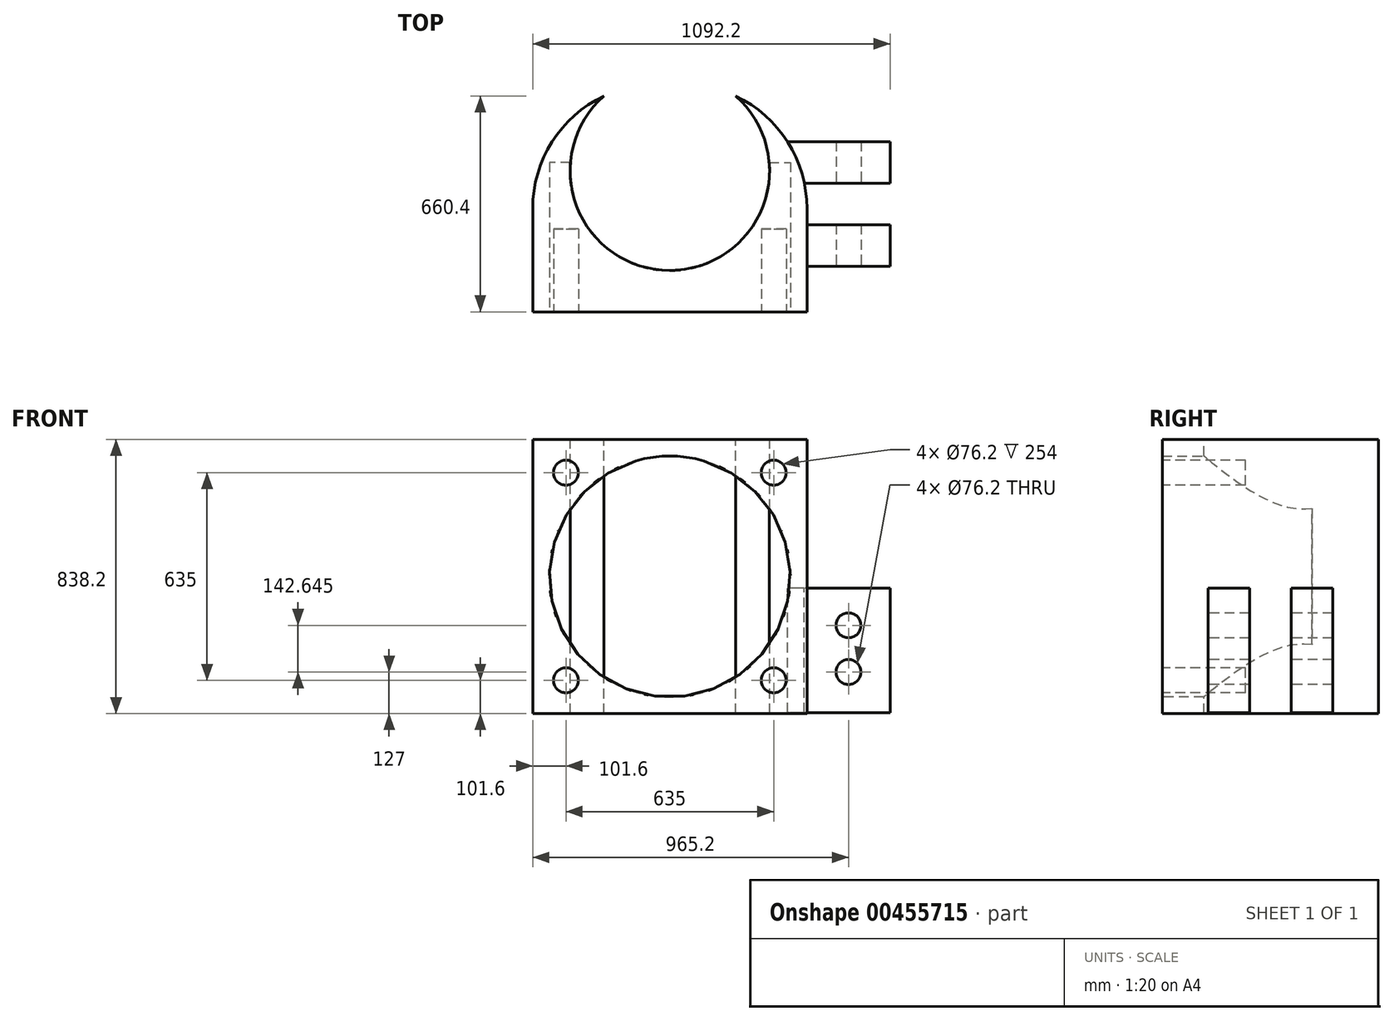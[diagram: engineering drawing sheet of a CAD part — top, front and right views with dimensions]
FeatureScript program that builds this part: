
annotation { "Feature Type Name" : "Feature", "Feature Type Description" : "" }
export const myFeature = defineFeature(function(context is Context, id is Id, definition is map)
    precondition{}
    {
        {
            var Q0;
            Q0=qCreatedBy(makeId("Front.planeOp"),FACE);
            var sketch = newSketch(context, id + "F0", { "sketchPlane" : qUnion([Q0])});
            skLineSegment(sketch, "E0.bottom", {"start": v(-419.1, 419.1) * mm, "end": v(419.1, 419.1) * mm});
            skLineSegment(sketch, "E0.top", {"start": v(-419.1, -419.1) * mm, "end": v(419.1, -419.1) * mm});
            skLineSegment(sketch, "E0.left", {"start": v(-419.1, 419.1) * mm, "end": v(-419.1, -419.1) * mm});
            skLineSegment(sketch, "E0.right", {"start": v(419.1, 419.1) * mm, "end": v(419.1, -419.1) * mm});
            skPoint(sketch, "E0.middle", {"position": v(0, 0) * mm});
            skCircle(sketch, "E1", {"center": v(-317.5, -317.5) * mm, "radius": 38.1 * mm});
            skCircle(sketch, "E2", {"center": v(317.5, -317.5) * mm, "radius": 38.1 * mm});
            skCircle(sketch, "E3", {"center": v(-317.5, 317.5) * mm, "radius": 38.1 * mm});
            skCircle(sketch, "E4", {"center": v(317.5, 317.5) * mm, "radius": 38.1 * mm});
            skSolve(sketch);
        }
        {
            var Q0;
            Q0=makeQuery(id+"F0.imprint","IMPRINT",FACE,{"disambiguationData":[TD([[makeQuery(id+"F0.imprint","IMPRINT",EDGE,{"derivedFrom":sQuery(id+"F0.wireOp",EDGE,"E3")}),1.0]])]});
            var Q1;
            Q1=makeQuery(id+"F0.imprint","IMPRINT",FACE,{"disambiguationData":[TD([[makeQuery(id+"F0.imprint","IMPRINT",EDGE,{"derivedFrom":sQuery(id+"F0.wireOp",EDGE,"E1")}),1.0]])]});
            var Q2;
            Q2=makeQuery(id+"F0.imprint","IMPRINT",FACE,{"disambiguationData":[TD([[makeQuery(id+"F0.imprint","IMPRINT",EDGE,{"derivedFrom":sQuery(id+"F0.wireOp",EDGE,"E2")}),1.0]])]});
            var Q3;
            Q3=makeQuery(id+"F0.imprint","IMPRINT",FACE,{"disambiguationData":[TD([[makeQuery(id+"F0.imprint","IMPRINT",EDGE,{"derivedFrom":sQuery(id+"F0.wireOp",EDGE,"E0.bottom")}),-1.0]])]});
            var Q4;
            Q4=makeQuery(id+"F0.imprint","IMPRINT",FACE,{"disambiguationData":[TD([[makeQuery(id+"F0.imprint","IMPRINT",EDGE,{"derivedFrom":sQuery(id+"F0.wireOp",EDGE,"E4")}),1.0]])]});
            extrude(context, id + "F1", {"entities" : qUnion([Q0, Q1, Q2, Q3, Q4]), "oppositeDirection" : true, "depth" : 660.4 * mm});
        }
        {
            var Q0;
            Q0=makeQuery(id+"F0.imprint","IMPRINT",FACE,{"disambiguationData":[TD([[makeQuery(id+"F0.imprint","IMPRINT",EDGE,{"derivedFrom":sQuery(id+"F0.wireOp",EDGE,"E2")}),1.0]])]});
            var Q1;
            Q1=makeQuery(id+"F0.imprint","IMPRINT",FACE,{"disambiguationData":[TD([[makeQuery(id+"F0.imprint","IMPRINT",EDGE,{"derivedFrom":sQuery(id+"F0.wireOp",EDGE,"E1")}),1.0]])]});
            var Q2;
            Q2=makeQuery(id+"F0.imprint","IMPRINT",FACE,{"disambiguationData":[TD([[makeQuery(id+"F0.imprint","IMPRINT",EDGE,{"derivedFrom":sQuery(id+"F0.wireOp",EDGE,"E3")}),1.0]])]});
            var Q3;
            Q3=makeQuery(id+"F0.imprint","IMPRINT",FACE,{"disambiguationData":[TD([[makeQuery(id+"F0.imprint","IMPRINT",EDGE,{"derivedFrom":sQuery(id+"F0.wireOp",EDGE,"E4")}),1.0]])]});
            extrude(context, id + "F2", {"entities" : qUnion([Q0, Q1, Q2, Q3]), "operationType" : NewBodyOperationType.REMOVE, "oppositeDirection" : true, "depth" : 254 * mm});
        }
        {
            var Q0;
            Q0=qCreatedBy(makeId("Top.planeOp"),FACE);
            var sketch = newSketch(context, id + "F3", { "sketchPlane" : qUnion([Q0])});
            skCircle(sketch, "E5", {"center": v(0, 431.8) * mm, "radius": 304.8 * mm});
            skSolve(sketch);
        }
        {
            var Q0;
            Q0 = qSketchRegion(id + "F3", true);
            extrude(context, id + "F4", {"entities" : qUnion([Q0]), "operationType" : NewBodyOperationType.REMOVE, "endBound" : BoundingType.SYMMETRIC, "oppositeDirection" : true, "depth" : 1016 * mm});
        }
        {
            var Q0;
            Q0=makeQuery(id+"F1.opExtrude","SWEPT_FACE",FACE,{"disambiguationData":[OSD([sQuery(id+"F0.wireOp",EDGE,"E0.right")])]});
            var sketch = newSketch(context, id + "F5", { "sketchPlane" : qUnion([Q0])});
            skLineSegment(sketch, "E6.bottom", {"start": v(139.7, -35.16) * mm, "end": v(266.7, -35.16) * mm});
            skLineSegment(sketch, "E6.top", {"start": v(139.7, -416.16) * mm, "end": v(266.7, -416.16) * mm});
            skLineSegment(sketch, "E6.left", {"start": v(139.7, -35.16) * mm, "end": v(139.7, -416.16) * mm});
            skLineSegment(sketch, "E6.right", {"start": v(266.7, -35.16) * mm, "end": v(266.7, -416.16) * mm});
            skLineSegment(sketch, "E7.bottom", {"start": v(393.7, -35.45) * mm, "end": v(520.7, -35.45) * mm});
            skLineSegment(sketch, "E7.top", {"start": v(393.7, -416.45) * mm, "end": v(520.7, -416.45) * mm});
            skLineSegment(sketch, "E7.left", {"start": v(393.7, -35.45) * mm, "end": v(393.7, -416.45) * mm});
            skLineSegment(sketch, "E7.right", {"start": v(520.7, -35.45) * mm, "end": v(520.7, -416.45) * mm});
            skSolve(sketch);
        }
        {
            var Q0;
            Q0 = qSketchRegion(id + "F5", true);
            extrude(context, id + "F6", {"entities" : qUnion([Q0]), "operationType" : NewBodyOperationType.ADD, "depth" : 254 * mm});
        }
        {
            var Q0;
            Q0=makeQuery(id+"F6.boolean.opBoolean","MERGE",FACE,{"derivedFrom":[makeQuery(id+"F1.opExtrude","CAP_FACE",FACE,{"disambiguationData":[OSD([sQuery(id+"F0.wireOp",EDGE,"E0.bottom"),sQuery(id+"F0.wireOp",EDGE,"E0.top"),sQuery(id+"F0.wireOp",EDGE,"E0.left"),sQuery(id+"F0.wireOp",EDGE,"E0.right")])],"isStart":true}),makeQuery(id+"F6.opExtrude","SWEPT_FACE",FACE,{"disambiguationData":[OSD([sQuery(id+"F5.wireOp",EDGE,"A37K3LjD-fdS7-IP0H-RDSH-3OM5a4bVXMQf.left")])]})]});
            var sketch = newSketch(context, id + "F7", { "sketchPlane" : qUnion([Q0])});
            skCircle(sketch, "E8", {"center": v(546.1, -149.46) * mm, "radius": 38.1 * mm});
            skCircle(sketch, "E9", {"center": v(546.1, -292.1) * mm, "radius": 38.1 * mm});
            skSolve(sketch);
        }
        {
            var Q0;
            Q0 = qSketchRegion(id + "F7", true);
            extrude(context, id + "F8", {"entities" : qUnion([Q0]), "operationType" : NewBodyOperationType.REMOVE, "oppositeDirection" : true, "depth" : 734.06 * mm});
        }
        {
            var Q0;
            Q0=makeQuery(id+"F0.imprint","IMPRINT",FACE,{"disambiguationData":[TD([[makeQuery(id+"F0.imprint","IMPRINT",EDGE,{"derivedFrom":sQuery(id+"F0.wireOp",EDGE,"E0.bottom")}),-1.0]])]});
            var sketch = newSketch(context, id + "F9", { "sketchPlane" : qUnion([Q0])});
            skCircle(sketch, "E10", {"center": v(0, 0) * mm, "radius": 368.3 * mm});
            skSolve(sketch);
        }
        {
            var Q0;
            Q0 = qSketchRegion(id + "F9", true);
            extrude(context, id + "F10", {"entities" : qUnion([Q0]), "operationType" : NewBodyOperationType.REMOVE, "oppositeDirection" : true, "depth" : 457.2 * mm});
        }
        {
            var Q0;
            Q0=makeQuery(id+"F1.opExtrude","CAP_EDGE",EDGE,{"disambiguationData":[OSD([sQuery(id+"F0.wireOp",EDGE,"E0.right")])],"isStart":false});
            fillet(context, id + "F11", {"entities" : qUnion([Q0]), "radius" : 381 * mm, "tangentPropagation" : true, "allowEdgeOverflow" : false});
        }
        {
            var Q0;
            Q0=makeQuery(id+"F1.opExtrude","CAP_EDGE",EDGE,{"disambiguationData":[OSD([sQuery(id+"F0.wireOp",EDGE,"E0.left")])],"isStart":false});
            fillet(context, id + "F12", {"entities" : qUnion([Q0]), "radius" : 381 * mm, "tangentPropagation" : true, "allowEdgeOverflow" : false});
        }
        {
            var Q0;
            Q0=makeQuery(id+"F9.imprint","IMPRINT",FACE,{"disambiguationData":[TD([[makeQuery(id+"F9.imprint","IMPRINT",EDGE,{"derivedFrom":sQuery(id+"F9.wireOp",EDGE,"E10")}),1.0]])]});
            cPlane(context, id + "F13", {"entities" : qUnion([Q0]), "cplaneType" : CPlaneType.OFFSET, "offset" : 457.2 * mm, "oppositeDirection" : true, "width" : 152.4 * mm, "height" : 152.4 * mm});
        }
        {
            var Q0;
            Q0=qCreatedBy(id+"F13.planeOp",FACE);
            var sketch = newSketch(context, id + "F14", { "sketchPlane" : qUnion([Q0])});
            skCircle(sketch, "E11", {"center": v(0, 39.74) * mm, "radius": 330.2 * mm});
            skSolve(sketch);
        }
        {
            var Q1;
            Q1=makeQuery(id+"F9.imprint","IMPRINT",FACE,{"disambiguationData":[TD([[makeQuery(id+"F9.imprint","IMPRINT",EDGE,{"derivedFrom":sQuery(id+"F9.wireOp",EDGE,"E10")}),1.0]])]});
            var Q2;
            Q2=makeQuery(id+"F14.imprint","IMPRINT",FACE,{"disambiguationData":[TD([[makeQuery(id+"F14.imprint","IMPRINT",EDGE,{"derivedFrom":sQuery(id+"F14.wireOp",EDGE,"E11")}),1.0]])]});
            loft(context, id + "F15", {"operationType" : NewBodyOperationType.REMOVE, "sheetProfilesArray" : [{ "sheetProfileEntities" : qUnion([Q1]) }, { "sheetProfileEntities" : qUnion([Q2]) }]});
        }
    });
